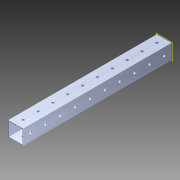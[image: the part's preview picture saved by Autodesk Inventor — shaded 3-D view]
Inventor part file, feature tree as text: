
AUTODESK INVENTOR PART (.ipt)
format: ipt  version: 2014 (Build 180170000, 170)  size: 1,232,384 bytes
history: native  units: in
note: dims shown in document units (in); Inventor stores cm internally (conversion verified against a paired STEP export)
features: extrude x3, sketch x3, pattern_circular x1, other x1, plane x1, imported_body x1
ambient origin geometry x8: Origin, YZ Plane, XZ Plane, XY Plane, X Axis, Y Axis, Z Axis, Center Point
bodies: Body1 (feature_tree)
feature tree (10):
  pattern_circular  "CirPattern2"
  other  "217-3426-STEP1"
  plane  "Work Plane1"
  extrude  "Extrusion1"  Depth=3937.0079in TaperAngle=0.0deg
  extrude  "Extrusion2"  Depth=10.0in TaperAngle=0.0deg
  extrude  "Extrusion3"  [1 undecoded]
  imported_body  "Base1"
  sketch  "Sketch1"  dims[d0=-21.0in d1=3937.0079in d2=0.0in]
  sketch  "Sketch3"  dims[d3=1.0in d4=0.0in d5=10.0in d6=0.0in]
  sketch  "Sketch4"
note: 1 required parameter value undecoded (feature->parameter linkage not recoverable at this tier; creation-order binding heuristic only, values carry confidence <= 0.55)
